# Revit family: LOROWERK 00200-DD0X
name_source: partatom
category: Pipe Fittings
revit_build: Autodesk Revit 2017 (Build: 20160225_1515(x64)
units: mm (PartAtom-declared; Revit-internal decimal feet)

## family parameters
Always vertical = Yes
Cut with Voids When Loaded = No
Part Type = Tee
Round Connector Dimension = Use Diameter
Shared = No
Work Plane-Based = No

## types (1)
- LOROWERK 00200-DD0X
    BIM = https://media.stage.bim.site
    Benennung = LORO-X Abzweig 87°, DN100/100
    Brandschutzklasse = B1 nach DIN 4102
    CONNECTOR0_DIAMETER_dX_0r = 100 mm  [stored 0.328084 ft]
    CONNECTOR0_dX_00 = 86 mm
    CONNECTOR0_dX_01 = 160 mm
    CONNECTOR0_ref_dX = 86 mm
    CONNECTOR1_DIAMETER_dNBN0_0r = 100 mm  [stored 0.328084 ft]
    CONNECTOR1_dNBN0_00 = 160 mm
    CONNECTOR1_dNBN0_01 = 86 mm
    CONNECTOR1_ref_dNBN0 = 86 mm
    CONNECTOR2_DIAMETER_dX_0r = 100 mm  [stored 0.328084 ft]
    CONNECTOR2_dX_00 = 140 mm
    CONNECTOR2_dX_01 = 66 mm
    CONNECTOR2_ref_dX = 66 mm
    DATANORM = 00200.DD0X
    Description = LORO-X Stahlabflussrohre
    Formstück-Gewicht [kg] = 2
    GTIN = 4038088013236
    HAN = 00200.DD0X
    HeinzeBIM = https://www.heinze.de
    Index = 20
    Index Number = 3
    LOROWERK 00200.DD0X en Visibility = Yes
    Manufacturer = LOROWERK K.H. Vahlbrauk GmbH & Co. KG
    Nenndruck = 0.5
    Nenndrucksystem = PN
    Nennweitensystem = DN
    Normen/Regeln/Zulassungen = DVGW für Trinkwasser
    Produktbezeichnung = Entsorgung
    Produktbezeichnung Text = LORO-X Stahlabflussrohre
    Produktkennung = Formstück
    Produktname = LORO-X Abzweig 87°
    Produktvideo = https://media.stage.bim.site
    Querschnittsform = rund
    Type Name = LORO-X Abzweig 87°
    VDIBSN = 020001???001001???00100100000100300700000000000120000000000000000003
    Verbindungsart I = Pressen
    Verbindungsart II = axial pressen
    Verlegeart = Unterputz
    max. zul. Dauer-Betriebstemperatur [°C] = 95

note: [stored X ft] marks values corroborated as IEEE doubles in the binary element streams (Revit-internal decimal feet)

## geometry (parser evidence)
native form markers: Blend x2
no freeform markers — native parametric forms only
